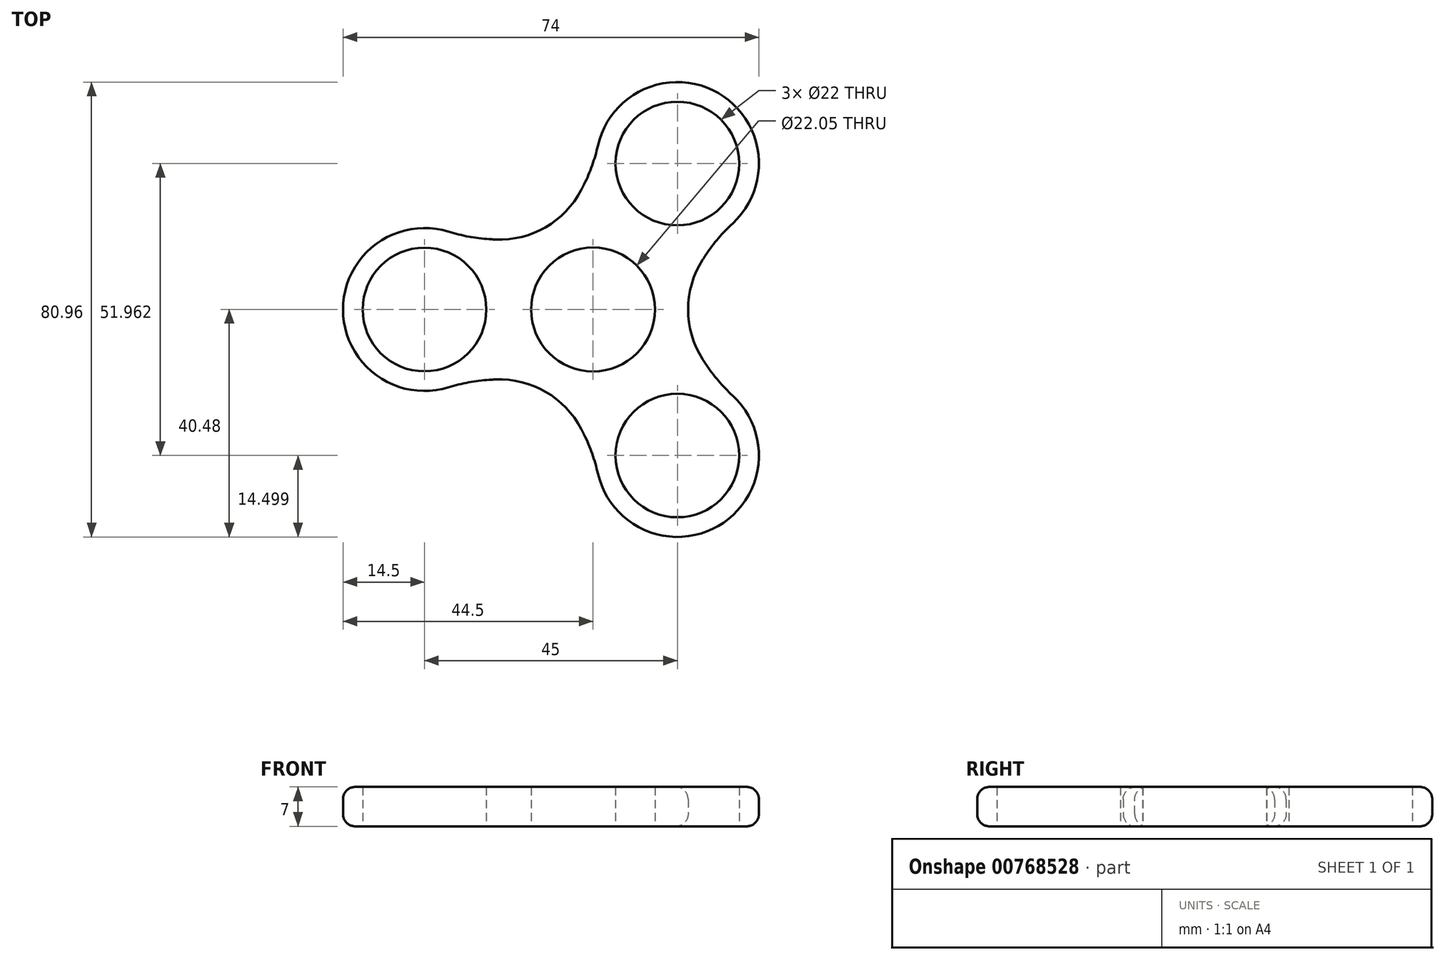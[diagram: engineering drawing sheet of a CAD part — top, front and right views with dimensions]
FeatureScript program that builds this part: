
annotation { "Feature Type Name" : "Feature", "Feature Type Description" : "" }
export const myFeature = defineFeature(function(context is Context, id is Id, definition is map)
    precondition{}
    {
        {
            var Q0;
            Q0=qCreatedBy(makeId("Top.planeOp"),FACE);
            var sketch = newSketch(context, id + "F0", { "sketchPlane" : qUnion([Q0])});
            skCircle(sketch, "E0", {"center": v(0, 0) * mm, "radius": 11.03 * mm});
            skLineSegment(sketch, "E1", {"start": v(0, 0) * mm, "end": v(-30, 0) * mm});
            skCircle(sketch, "E2", {"center": v(-30, 0) * mm, "radius": 11 * mm});
            skCircle(sketch, "E3", {"center": v(-30, 0) * mm, "radius": 14.5 * mm});
            skCircle(sketch, "E4", {"center": v(0, 0) * mm, "radius": 14.5 * mm});
            skArc(sketch, "E5", {"start": v(0, -14.5) * mm, "mid": v(-15, -12.4) * mm, "end": v(-30, -14.5) * mm});
            skArc(sketch, "E6.MirrorCS", {"start": v(0, 14.5) * mm, "mid": v(-15, 12.4) * mm, "end": v(-30, 14.5) * mm});
            skSolve(sketch);
        }
        {
            var Q0;
            Q0=qSketchRegion(id+"F0",true);
            extrude(context, id + "F1", {"entities" : qUnion([Q0]), "depth" : 7 * mm, "offsetDistance" : 25 * mm});
        }
        {
            var Q0;
            Q0=makeQuery(id+"F1.opExtrude","SWEPT_BODY",BODY,{"disambiguationData":[OSD([sQuery(id+"F0.wireOp",EDGE,"E0"),sQuery(id+"F0.wireOp",EDGE,"E2"),sQuery(id+"F0.wireOp",EDGE,"E3"),sQuery(id+"F0.wireOp",EDGE,"E4"),sQuery(id+"F0.wireOp",EDGE,"E5"),sQuery(id+"F0.wireOp",EDGE,"E6.MirrorCS")])]});
            var Q1;
            Q1=makeQuery(id+"F1.opExtrude","SWEPT_FACE",FACE,{"disambiguationData":[OSD([sQuery(id+"F0.wireOp",EDGE,"E4")])]});
            circularPattern(context, id + "F2", {"entities" : qUnion([Q0]), "axis" : qUnion([Q1]), "angle" : 360 * degree, "instanceCount" : 3, "equalSpace" : true});
        }
        {
            var Q0;
            Q0=makeQuery(id+"F1.opExtrude","SWEPT_BODY",BODY,{"disambiguationData":[OSD([sQuery(id+"F0.wireOp",EDGE,"E0"),sQuery(id+"F0.wireOp",EDGE,"E2"),sQuery(id+"F0.wireOp",EDGE,"E3"),sQuery(id+"F0.wireOp",EDGE,"E4"),sQuery(id+"F0.wireOp",EDGE,"E5"),sQuery(id+"F0.wireOp",EDGE,"E6.MirrorCS")])]});
            var Q1;
            Q1=makeQuery(id+"F2.opPattern","COPY",BODY,{"derivedFrom":makeQuery(id+"F1.opExtrude","SWEPT_BODY",BODY,{"disambiguationData":[OSD([sQuery(id+"F0.wireOp",EDGE,"E0"),sQuery(id+"F0.wireOp",EDGE,"E2"),sQuery(id+"F0.wireOp",EDGE,"E3"),sQuery(id+"F0.wireOp",EDGE,"E4"),sQuery(id+"F0.wireOp",EDGE,"E5"),sQuery(id+"F0.wireOp",EDGE,"E6.MirrorCS")])]}),"instanceName":"1"});
            var Q2;
            Q2=makeQuery(id+"F2.opPattern","COPY",BODY,{"derivedFrom":makeQuery(id+"F1.opExtrude","SWEPT_BODY",BODY,{"disambiguationData":[OSD([sQuery(id+"F0.wireOp",EDGE,"E0"),sQuery(id+"F0.wireOp",EDGE,"E2"),sQuery(id+"F0.wireOp",EDGE,"E3"),sQuery(id+"F0.wireOp",EDGE,"E4"),sQuery(id+"F0.wireOp",EDGE,"E5"),sQuery(id+"F0.wireOp",EDGE,"E6.MirrorCS")])]}),"instanceName":"2"});
            booleanBodies(context, id + "F3", {"operationType" : BooleanOperationType.UNION, "tools" : qUnion([Q0, Q1, Q2])});
        }
        {
            var Q0;
            Q0=makeQuery(id+"F3.opBoolean","INTERSECT",EDGE,{"derivedFrom":[makeQuery(id+"F2.opPattern","COPY",FACE,{"derivedFrom":makeQuery(id+"F1.opExtrude","SWEPT_FACE",FACE,{"disambiguationData":[OSD([sQuery(id+"F0.wireOp",EDGE,"E6.MirrorCS")])]}),"instanceName":"1"}),makeQuery(id+"F2.opPattern","COPY",FACE,{"derivedFrom":makeQuery(id+"F1.opExtrude","SWEPT_FACE",FACE,{"disambiguationData":[OSD([sQuery(id+"F0.wireOp",EDGE,"E5")])]}),"instanceName":"2"})]});
            var Q1;
            Q1=makeQuery(id+"F3.opBoolean","INTERSECT",EDGE,{"derivedFrom":[makeQuery(id+"F1.opExtrude","SWEPT_FACE",FACE,{"disambiguationData":[OSD([sQuery(id+"F0.wireOp",EDGE,"E6.MirrorCS")])]}),makeQuery(id+"F2.opPattern","COPY",FACE,{"derivedFrom":makeQuery(id+"F1.opExtrude","SWEPT_FACE",FACE,{"disambiguationData":[OSD([sQuery(id+"F0.wireOp",EDGE,"E5")])]}),"instanceName":"1"})]});
            var Q2;
            Q2=makeQuery(id+"F3.opBoolean","INTERSECT",EDGE,{"derivedFrom":[makeQuery(id+"F1.opExtrude","SWEPT_FACE",FACE,{"disambiguationData":[OSD([sQuery(id+"F0.wireOp",EDGE,"E5")])]}),makeQuery(id+"F2.opPattern","COPY",FACE,{"derivedFrom":makeQuery(id+"F1.opExtrude","SWEPT_FACE",FACE,{"disambiguationData":[OSD([sQuery(id+"F0.wireOp",EDGE,"E6.MirrorCS")])]}),"instanceName":"2"})]});
            fillet(context, id + "F4", {"entities" : qUnion([Q0, Q1, Q2]), "radius" : 16.4 * mm, "tangentPropagation" : true, "allowEdgeOverflow" : false});
        }
        {
            var Q0;
            Q0=makeQuery(id+"F1.opExtrude","SWEPT_EDGE",EDGE,{"disambiguationData":[OSD([sQuery(id+"F0.wireOp",EDGE,"E3"),sQuery(id+"F0.wireOp",EDGE,"E6.MirrorCS")])]});
            var Q1;
            Q1=makeQuery(id+"F2.opPattern","COPY",EDGE,{"derivedFrom":makeQuery(id+"F1.opExtrude","SWEPT_EDGE",EDGE,{"disambiguationData":[OSD([sQuery(id+"F0.wireOp",EDGE,"E3"),sQuery(id+"F0.wireOp",EDGE,"E5")])]}),"instanceName":"1"});
            var Q2;
            Q2=makeQuery(id+"F2.opPattern","COPY",EDGE,{"derivedFrom":makeQuery(id+"F1.opExtrude","SWEPT_EDGE",EDGE,{"disambiguationData":[OSD([sQuery(id+"F0.wireOp",EDGE,"E3"),sQuery(id+"F0.wireOp",EDGE,"E6.MirrorCS")])]}),"instanceName":"1"});
            var Q3;
            Q3=makeQuery(id+"F2.opPattern","COPY",EDGE,{"derivedFrom":makeQuery(id+"F1.opExtrude","SWEPT_EDGE",EDGE,{"disambiguationData":[OSD([sQuery(id+"F0.wireOp",EDGE,"E3"),sQuery(id+"F0.wireOp",EDGE,"E5")])]}),"instanceName":"2"});
            var Q4;
            Q4=makeQuery(id+"F1.opExtrude","SWEPT_EDGE",EDGE,{"disambiguationData":[OSD([sQuery(id+"F0.wireOp",EDGE,"E3"),sQuery(id+"F0.wireOp",EDGE,"E5")])]});
            var Q5;
            Q5=makeQuery(id+"F2.opPattern","COPY",EDGE,{"derivedFrom":makeQuery(id+"F1.opExtrude","SWEPT_EDGE",EDGE,{"disambiguationData":[OSD([sQuery(id+"F0.wireOp",EDGE,"E3"),sQuery(id+"F0.wireOp",EDGE,"E6.MirrorCS")])]}),"instanceName":"2"});
            fillet(context, id + "F5", {"entities" : qUnion([Q0, Q1, Q2, Q3, Q4, Q5]), "radius" : 30.91 * mm, "tangentPropagation" : true, "allowEdgeOverflow" : false});
        }
        {
            var Q0;
            Q0=makeQuery(id+"F2.opPattern","COPY",EDGE,{"derivedFrom":makeQuery(id+"F1.opExtrude","CAP_EDGE",EDGE,{"disambiguationData":[OSD([sQuery(id+"F0.wireOp",EDGE,"E3")])],"isStart":false}),"instanceName":"2"});
            var Q1;
            {var subQ0=sQuery(id+"F0.wireOp",EDGE,"E6.MirrorCS");var subQ1=sQuery(id+"F0.wireOp",EDGE,"E5");var subQ2=makeQuery(id+"F1.opExtrude","CAP_FACE",FACE,{"disambiguationData":[OSD([sQuery(id+"F0.wireOp",EDGE,"E0"),sQuery(id+"F0.wireOp",EDGE,"E2"),sQuery(id+"F0.wireOp",EDGE,"E3"),sQuery(id+"F0.wireOp",EDGE,"E4"),subQ1,subQ0])],"isStart":true});Q1=makeQuery(id+"F4.opFillet","BLEND_EDGE",EDGE,{"blendedFrom":[makeQuery(id+"F3.opBoolean","INTERSECT",EDGE,{"derivedFrom":[makeQuery(id+"F1.opExtrude","SWEPT_FACE",FACE,{"disambiguationData":[OSD([subQ1])]}),makeQuery(id+"F2.opPattern","COPY",FACE,{"derivedFrom":makeQuery(id+"F1.opExtrude","SWEPT_FACE",FACE,{"disambiguationData":[OSD([subQ0])]}),"instanceName":"2"})]}),makeQuery(id+"F3.opBoolean","MERGE",FACE,{"derivedFrom":[subQ2,makeQuery(id+"F2.opPattern","COPY",FACE,{"derivedFrom":subQ2,"instanceName":"1"}),makeQuery(id+"F2.opPattern","COPY",FACE,{"derivedFrom":subQ2,"instanceName":"2"})]})],"blendedInto":[makeQuery(id+"F3.opBoolean","MERGE",FACE,{"derivedFrom":[subQ2,makeQuery(id+"F2.opPattern","COPY",FACE,{"derivedFrom":subQ2,"instanceName":"1"}),makeQuery(id+"F2.opPattern","COPY",FACE,{"derivedFrom":subQ2,"instanceName":"2"})]})]});}
            var Q2;
            Q2=makeQuery(id+"F2.opPattern","COPY",EDGE,{"derivedFrom":makeQuery(id+"F1.opExtrude","CAP_EDGE",EDGE,{"disambiguationData":[OSD([sQuery(id+"F0.wireOp",EDGE,"E6.MirrorCS")])],"isStart":true}),"instanceName":"2"});
            fillet(context, id + "F6", {"entities" : qUnion([Q0, Q1, Q2]), "radius" : 2.17 * mm, "tangentPropagation" : true, "allowEdgeOverflow" : false});
        }
    });
